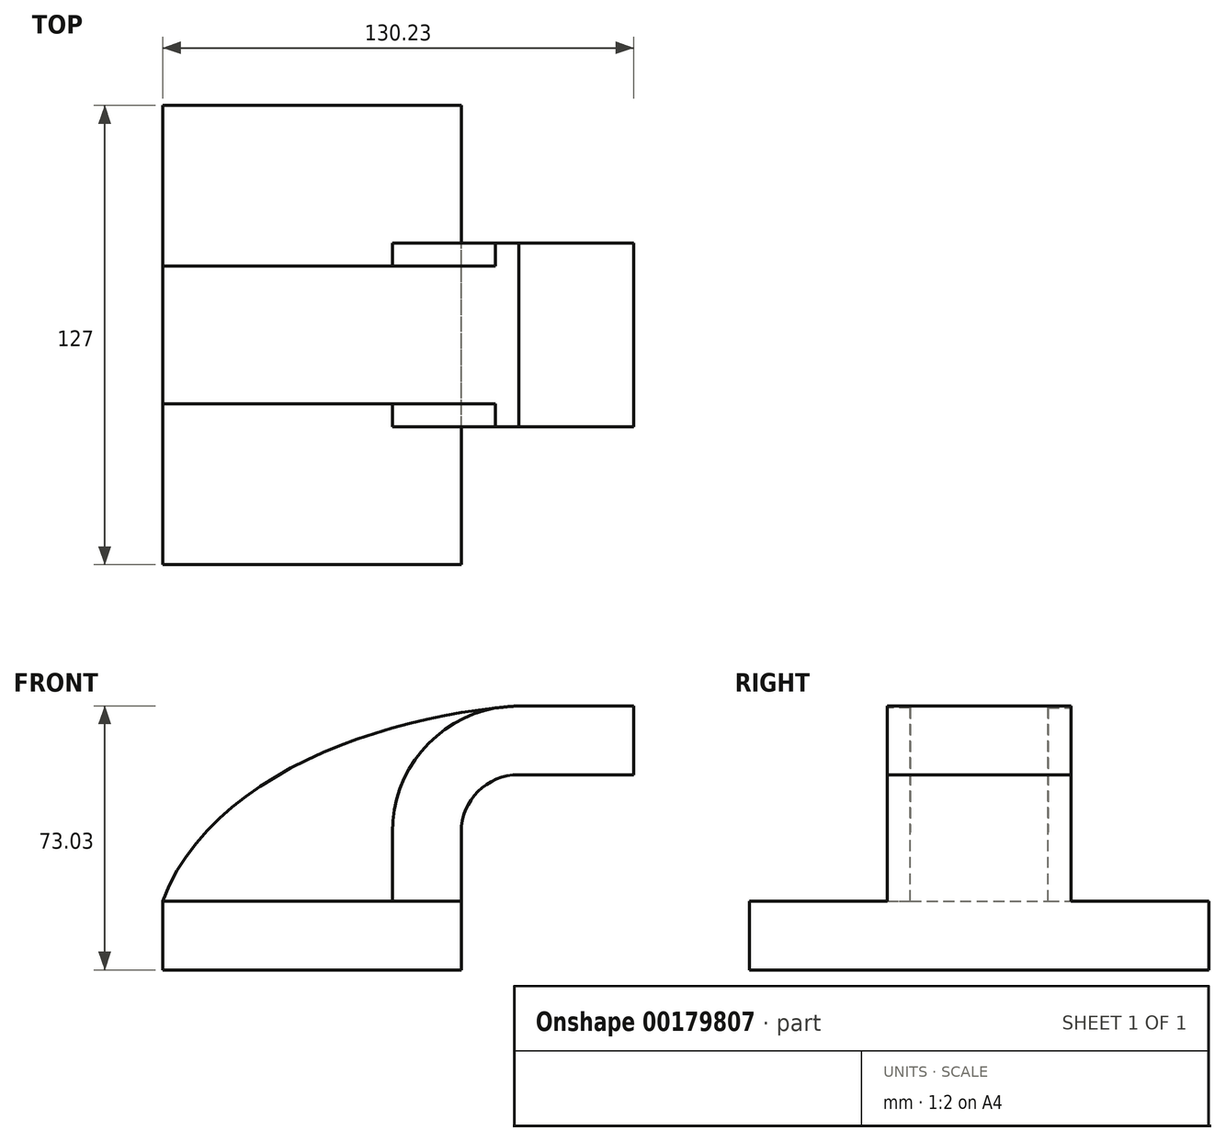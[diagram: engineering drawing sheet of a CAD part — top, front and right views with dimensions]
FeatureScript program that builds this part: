
annotation { "Feature Type Name" : "Feature", "Feature Type Description" : "" }
export const myFeature = defineFeature(function(context is Context, id is Id, definition is map)
    precondition{}
    {
        {
            var Q0;
            Q0=qCreatedBy(makeId("Front.planeOp"),FACE);
            var sketch = newSketch(context, id + "F0", { "sketchPlane" : qUnion([Q0])});
            skLineSegment(sketch, "E0.bottom", {"start": v(-41.28, 9.52) * mm, "end": v(41.27, 9.53) * mm});
            skLineSegment(sketch, "E0.top", {"start": v(-41.28, -9.53) * mm, "end": v(41.28, -9.53) * mm});
            skLineSegment(sketch, "E0.left", {"start": v(-41.28, 9.52) * mm, "end": v(-41.27, -9.53) * mm});
            skLineSegment(sketch, "E0.right", {"start": v(41.28, 9.53) * mm, "end": v(41.28, -9.52) * mm});
            skPoint(sketch, "E0.middle", {"position": v(0, 0) * mm});
            skLineSegment(sketch, "E1.right", {"start": v(104.86, 66.67) * mm, "end": v(104.86, 38.1) * mm});
            skPoint(sketch, "E1.middle", {"position": v(79.46, 52.39) * mm});
            skLineSegment(sketch, "E2", {"start": v(41.27, 9.53) * mm, "end": v(41.27, 28.58) * mm});
            skArc(sketch, "E3", {"start": v(41.27, 28.58) * mm, "mid": v(45.92, 39.8) * mm, "end": v(57.15, 44.45) * mm});
            skLineSegment(sketch, "E4", {"start": v(57.15, 44.45) * mm, "end": v(88.95, 44.45) * mm});
            skLineSegment(sketch, "E5.0", {"start": v(57.15, 63.5) * mm, "end": v(88.95, 63.5) * mm});
            skArc(sketch, "E5.1", {"start": v(22.23, 28.58) * mm, "mid": v(32.45, 53.27) * mm, "end": v(57.15, 63.5) * mm});
            skLineSegment(sketch, "E5.2", {"start": v(22.23, 9.53) * mm, "end": v(22.23, 28.58) * mm});
            skLineSegment(sketch, "E6", {"start": v(88.95, 44.45) * mm, "end": v(88.95, 63.5) * mm});
            skLineSegment(sketch, "E7", {"start": v(62.56, 66.67) * mm, "end": v(62.56, 38.1) * mm});
            skLineSegment(sketch, "E8", {"start": v(62.56, 66.67) * mm, "end": v(104.86, 66.67) * mm});
            skFitSpline(sketch, "E9", {"points": [v(-41.28, 9.52) * mm, v(57.15, 63.5) * mm], "startDerivative": vector(40.98, 107.45) * mm, "endDerivative": vector(108.34, 7.94) * mm});
            skLineSegment(sketch, "E10", {"start": v(62.56, 38.1) * mm, "end": v(104.86, 38.1) * mm});
            skSolve(sketch);
        }
        {
            var Q0;
            Q0=makeQuery(id+"F0.imprint","IMPRINT",FACE,{"disambiguationData":[TD([[makeQuery(id+"F0.imprint","IMPRINT",EDGE,{"derivedFrom":sQuery(id+"F0.wireOp",EDGE,"E0.top")}),1.0]])]});
            extrude(context, id + "F1", {"entities" : qUnion([Q0]), "endBound" : BoundingType.SYMMETRIC, "depth" : 127 * mm});
        }
        {
            var Q0;
            {var subQ4=sQuery(id+"F0.wireOp",EDGE,"E2");Q0=makeQuery(id+"F0.imprint","IMPRINT",FACE,{"disambiguationData":[TD([[makeQuery(id+"F0.imprint","IMPRINT",EDGE,{"derivedFrom":subQ4}),1.0]])]});}
            var Q1;
            {var subQ0=sQuery(id+"F0.wireOp",EDGE,"E6");Q1=makeQuery(id+"F0.imprint","IMPRINT",FACE,{"disambiguationData":[TD([[makeQuery(id+"F0.imprint","IMPRINT",EDGE,{"derivedFrom":subQ0}),1.0]])]});}
            extrude(context, id + "F2", {"entities" : qUnion([Q0, Q1]), "operationType" : NewBodyOperationType.ADD, "endBound" : BoundingType.SYMMETRIC, "depth" : 50.8 * mm});
        }
        {
            var Q0;
            {var subQ3=sQuery(id+"F0.wireOp",EDGE,"E5.2");Q0=makeQuery(id+"F0.imprint","IMPRINT",FACE,{"disambiguationData":[TD([[makeQuery(id+"F0.imprint","IMPRINT",EDGE,{"derivedFrom":subQ3}),1.0]])]});}
            extrude(context, id + "F3", {"entities" : qUnion([Q0]), "operationType" : NewBodyOperationType.ADD, "endBound" : BoundingType.SYMMETRIC, "depth" : 38.1 * mm});
        }
    });
